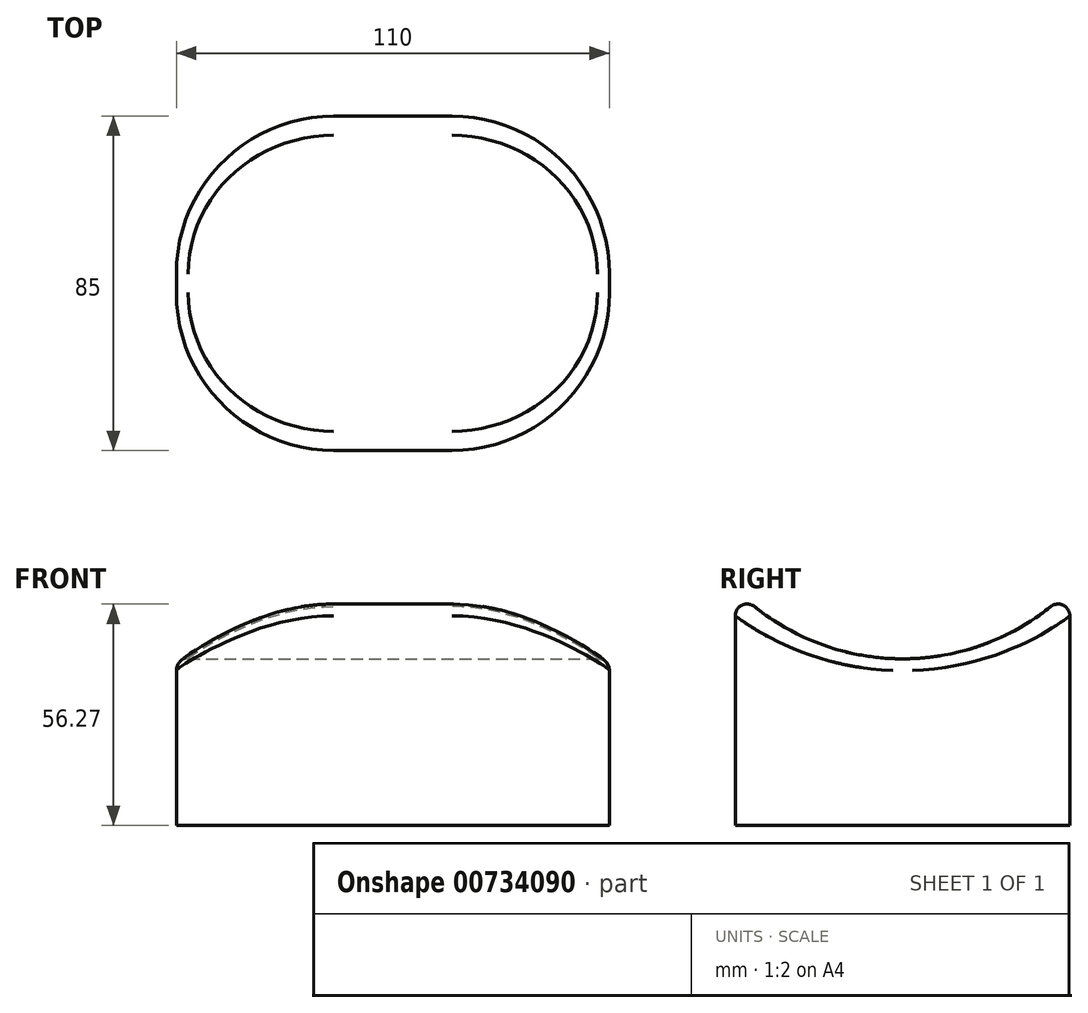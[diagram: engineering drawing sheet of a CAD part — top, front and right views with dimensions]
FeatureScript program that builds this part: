
annotation { "Feature Type Name" : "Feature", "Feature Type Description" : "" }
export const myFeature = defineFeature(function(context is Context, id is Id, definition is map)
    precondition{}
    {
        {
            var Q0;
            Q0=qCreatedBy(makeId("Top.planeOp"),FACE);
            var sketch = newSketch(context, id + "F0", { "sketchPlane" : qUnion([Q0])});
            skLineSegment(sketch, "E0.bottom", {"start": v(-15, 42.5) * mm, "end": v(15, 42.5) * mm});
            skLineSegment(sketch, "E0.top", {"start": v(-15, -42.5) * mm, "end": v(15, -42.5) * mm});
            skLineSegment(sketch, "E0.left", {"start": v(-55, 2.5) * mm, "end": v(-55, -2.5) * mm});
            skLineSegment(sketch, "E0.right", {"start": v(55, 2.5) * mm, "end": v(55, -2.5) * mm});
            skPoint(sketch, "E0.middle", {"position": v(0, 0) * mm});
            skPoint(sketch, "E1.visualSharp", {"position": v(-55, 42.5) * mm});
            skArc(sketch, "E1.filletArc", {"start": v(-15, 42.5) * mm, "mid": v(-43.28, 30.78) * mm, "end": v(-55, 2.5) * mm});
            skPoint(sketch, "E2.visualSharp", {"position": v(-55, -42.5) * mm});
            skArc(sketch, "E2.filletArc", {"start": v(-55, -2.5) * mm, "mid": v(-43.28, -30.78) * mm, "end": v(-15, -42.5) * mm});
            skPoint(sketch, "E3.visualSharp", {"position": v(55, -42.5) * mm});
            skArc(sketch, "E3.filletArc", {"start": v(15, -42.5) * mm, "mid": v(43.28, -30.78) * mm, "end": v(55, -2.5) * mm});
            skPoint(sketch, "E4.visualSharp", {"position": v(55, 42.5) * mm});
            skArc(sketch, "E4.filletArc", {"start": v(55, 2.5) * mm, "mid": v(43.28, 30.78) * mm, "end": v(15, 42.5) * mm});
            skSolve(sketch);
        }
        {
            var Q0;
            Q0=makeQuery(id+"F0.imprint","IMPRINT",FACE,{"disambiguationData":[TD([[makeQuery(id+"F0.imprint","IMPRINT",EDGE,{"derivedFrom":sQuery(id+"F0.wireOp",EDGE,"E0.bottom")}),-1.0]])]});
            extrude(context, id + "F1", {"entities" : qUnion([Q0]), "endBound" : BoundingType.SYMMETRIC, "depth" : 60 * mm, "offsetDistance" : 25 * mm});
        }
        {
            var Q0;
            Q0=qCreatedBy(makeId("Right.planeOp"),FACE);
            var sketch = newSketch(context, id + "F2", { "sketchPlane" : qUnion([Q0])});
            skLineSegment(sketch, "E5.0.2", {"start": v(42.5, 30) * mm, "end": v(-42.5, 30) * mm});
            skArc(sketch, "E6", {"start": v(-42.5, 30) * mm, "mid": v(0, 12.35) * mm, "end": v(42.5, 30) * mm});
            skSolve(sketch);
        }
        {
            var Q0;
            Q0=makeQuery(id+"F2.imprint","IMPRINT",FACE,{"disambiguationData":[TD([[makeQuery(id+"F2.imprint","IMPRINT",EDGE,{"derivedFrom":sQuery(id+"F2.wireOp",EDGE,"E5.0.2")}),1.0]])]});
            extrude(context, id + "F3", {"entities" : qUnion([Q0]), "operationType" : NewBodyOperationType.REMOVE, "endBound" : BoundingType.SYMMETRIC, "oppositeDirection" : true, "depth" : 160 * mm, "offsetDistance" : 25 * mm});
        }
        {
            var Q0;
            {var subQ0=sQuery(id+"F2.wireOp",EDGE,"E6");var subQ1=sQuery(id+"F2.wireOp",EDGE,"E5.0.2");Q0=makeQuery(id+"F3.boolean.opBoolean","MERGE",EDGE,{"derivedFrom":[makeQuery(id+"F1.opExtrude","CAP_EDGE",EDGE,{"disambiguationData":[OSD([sQuery(id+"F0.wireOp",EDGE,"E0.bottom")])],"isStart":false}),makeQuery(id+"F3.opExtrude","SWEPT_EDGE",EDGE,{"disambiguationData":[OSD([subQ1,subQ0]),TDD([makeQuery(id+"F2.imprint","INTERSECT",VERTEX,{"disambiguationData":[OD(0.0)],"derivedFrom":[subQ1,subQ0]})])]})]});}
            var Q1;
            Q1=makeQuery(id+"F3.boolean.opBoolean","INTERSECT",EDGE,{"derivedFrom":[makeQuery(id+"F1.opExtrude","SWEPT_FACE",FACE,{"disambiguationData":[OSD([sQuery(id+"F0.wireOp",EDGE,"E1.filletArc"),sQuery(id+"F0.wireOp",EDGE,"E2.filletArc")])]}),makeQuery(id+"F3.opExtrude","SWEPT_FACE",FACE,{"disambiguationData":[OSD([sQuery(id+"F2.wireOp",EDGE,"E6")])]})]});
            var Q2;
            {var subQ0=sQuery(id+"F2.wireOp",EDGE,"E6");var subQ1=sQuery(id+"F2.wireOp",EDGE,"E5.0.2");Q2=makeQuery(id+"F3.boolean.opBoolean","MERGE",EDGE,{"derivedFrom":[makeQuery(id+"F1.opExtrude","CAP_EDGE",EDGE,{"disambiguationData":[OSD([sQuery(id+"F0.wireOp",EDGE,"E0.top")])],"isStart":false}),makeQuery(id+"F3.opExtrude","SWEPT_EDGE",EDGE,{"disambiguationData":[OSD([subQ1,subQ0]),TDD([makeQuery(id+"F2.imprint","INTERSECT",VERTEX,{"disambiguationData":[OD(1.0)],"derivedFrom":[subQ1,subQ0]})])]})]});}
            var Q3;
            Q3=makeQuery(id+"F3.boolean.opBoolean","INTERSECT",EDGE,{"derivedFrom":[makeQuery(id+"F1.opExtrude","SWEPT_FACE",FACE,{"disambiguationData":[OSD([sQuery(id+"F0.wireOp",EDGE,"E3.filletArc"),sQuery(id+"F0.wireOp",EDGE,"E4.filletArc")])]}),makeQuery(id+"F3.opExtrude","SWEPT_FACE",FACE,{"disambiguationData":[OSD([sQuery(id+"F2.wireOp",EDGE,"E6")])]})]});
            fillet(context, id + "F4", {"entities" : qUnion([Q0, Q1, Q2, Q3]), "radius" : 3 * mm, "tangentPropagation" : true, "allowEdgeOverflow" : false});
        }
    });
